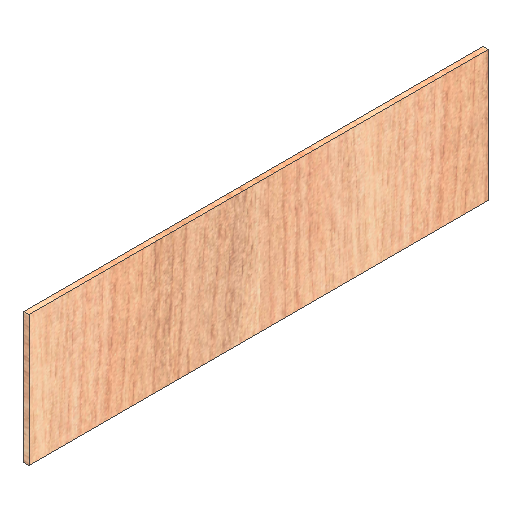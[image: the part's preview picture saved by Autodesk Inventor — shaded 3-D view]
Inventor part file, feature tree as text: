
AUTODESK INVENTOR PART (.ipt)
format: ipt  version: 2021 (Build 250183000, 183)  size: 258,560 bytes
history: native  units: mm
features: extrude x1, sketch x1
ambient origin geometry x8: Origin, YZ Plane, XZ Plane, XY Plane, X Axis, Y Axis, Z Axis, Center Point
bodies: Solid1 (feature_tree)
feature tree (2):
  extrude  "Extrusion1"  Depth=351.12mm
  sketch  "Sketch1"  dims[d0=100.0mm d1=351.12mm d2=4.0mm d3=0.0mm]
